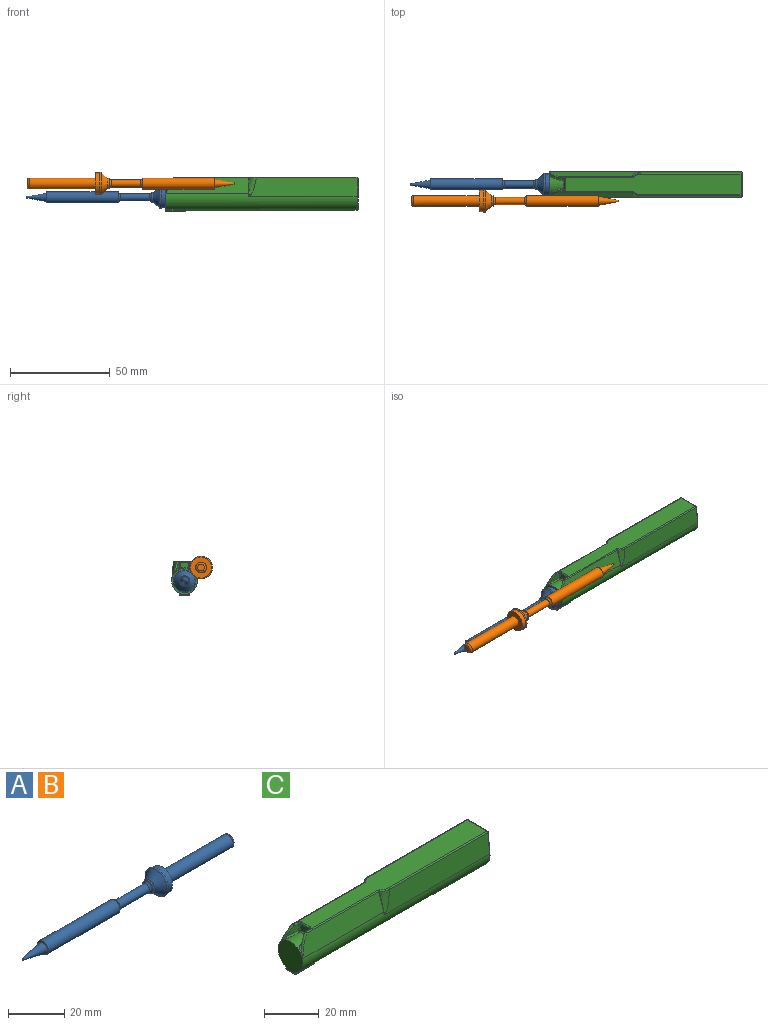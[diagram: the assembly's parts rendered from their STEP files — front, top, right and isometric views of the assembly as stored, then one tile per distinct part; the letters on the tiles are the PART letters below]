
ASSEMBLY  parts=3 mates=1
PART A: 15 faces, bbox 104.1x12.3x12.3 mm
  f0: plane 3.4x3.4mm, normal (1,0,0), area 9.1mm2, adj f12
  f1: cylinder r=2.7mm len=33mm, axis (1,0,0), area 559.8mm2, adj f2,f12
  f2: plane 10.6x10.6mm, normal (1,0,0), area 65.3mm2, adj f1,f3
  f3: cylinder r=5.3mm len=10.6mm, axis (1,0,0), area 74.9mm2, adj f2,f4
  f4: torus R=5.3mm, axis (1,0,0), area 43.9mm2, adj f3,f5
  f5: cone r=5.3mm half-angle=39.5deg, axis (1,0,0), area 104.8mm2, adj f4,f6
  f6: cylinder r=2.62mm len=5.25mm, axis (1,0,0), area 12.4mm2, adj f5,f13
  f7: cylinder r=1.8mm len=14.77mm, axis (1,0,0), area 167mm2, adj f13,f14
  f8: cylinder r=2.75mm len=36mm, axis (1,0,0), area 622mm2, adj f9,f14
  f9: plane 5.5x5.5mm, normal (-1,0,0), area 8.6mm2, adj f8,f10
  f10: cone r=2.2mm half-angle=10.3deg, axis (1,0,0), area 82.2mm2, adj f9,f11
  f11: sphere r=0.38mm, area 0.7mm2, adj f10
  f12: torus R=1.7mm, axis (-1,0,0), area 23.1mm2, adj f0,f1
  f13: torus R=2.8mm, axis (1,0,0), area 18.4mm2, adj f6,f7
  f14: torus R=2.8mm, axis (-1,0,0), area 20.5mm2, adj f7,f8
PART B: same geometry as A
PART C: 69 faces, bbox 98.5x14.5x21 mm
  f0: cylinder r=6.45mm len=96mm, axis (-1,0,0), area 2152.6mm2, adj f2,f4,f5,f6,f7,f8,f9,f11
  f1: plane 15.6x11.9mm, normal (1,0,0), area 162mm2, adj f46,f50,f52,f53
  f2: plane 13.25x12.9mm, normal (-1,0,0), area 132.7mm2, adj f0,f58,f64,f65
  f3: plane 9x4.25mm, normal (0,0,-1), area 38.2mm2, adj f59,f62,f65,f68
  f4: plane 9x0.91mm, normal (0,1,0), area 8.2mm2, adj f0,f63,f64,f68
  f5: plane 9x0.91mm, normal (0,-1,0), area 8.2mm2, adj f0,f57,f58,f59
  f6: plane 4.25x0.71mm, normal (1,0,0), area 2mm2, adj f0,f57,f62,f63
  f7: plane 41.55x7.98mm, normal (0,0.96,0.28), area 329.6mm2, adj f0,f20,f36,f37
  f8: plane 54.79x9.64mm, normal (0,-1,0.1), area 471.5mm2, adj f0,f14,f15,f53,f56
  f9: plane 54.25x9.1mm, normal (0,1,0.1), area 471.5mm2, adj f0,f12,f13,f45,f46
  f10: plane 91.14x10.09mm, normal (0,0,1), area 772.9mm2, adj f28,f31,f35,f36,f38,f39,f41,f42
  f11: plane 41.55x7.98mm, normal (0,-0.96,0.28), area 329.6mm2, adj f0,f19,f47,f48
  f12: bspline ~11.52x4.08mm, area 23.8mm2, adj f9,f13,f33,f37,f42
  f13: bspline ~1.61x0.7mm, area 0.2mm2, adj f9,f12,f29
  f14: bspline ~11.52x4.08mm, area 23.8mm2, adj f8,f15,f43,f47,f54
  f15: bspline ~1.61x0.7mm, area 0.2mm2, adj f8,f14,f40
  f16: plane 4.44x3.06mm, normal (-1,0,0), area 12.5mm2, adj f26,f27,f34,f35
  f17: cylinder r=10mm len=5.24mm, axis (0,0,1), area 12.3mm2, adj f19,f25,f34,f41
  f18: cylinder r=10mm len=5.24mm, axis (0,0,1), area 12.3mm2, adj f20,f22,f27,f28
  f19: bspline ~13.5x7.26mm, area 9.7mm2, adj f11,f17,f23,f44
  f20: bspline ~13.5x7.26mm, area 9.7mm2, adj f7,f18,f21,f32
  f21: bspline ~4.26x2.97mm, area 1.6mm2, adj f0,f20,f22
  f22: bspline ~5.95x2.06mm, area 5.4mm2, adj f0,f18,f21,f24
  f23: bspline ~4.26x2.97mm, area 1.6mm2, adj f0,f19,f25
  f24: sphere r=0.5mm, area 0.4mm2, adj f22,f26,f27
  f25: bspline ~5.95x2.06mm, area 5.4mm2, adj f0,f17,f23,f30
  f26: torus R=6.95mm, axis (-1,0,0), area 3.4mm2, adj f0,f16,f24,f30
  f27: cylinder r=0.5mm len=3.06mm, axis (0,0,1), area 2.5mm2, adj f16,f18,f24,f31
  f28: torus R=9.5mm, axis (0,0,-1), area 1.6mm2, adj f10,f18,f31,f32
  f29: bspline ~1.32x0.27mm, area 0mm2, adj f0,f13,f33
  f30: sphere r=0.5mm, area 0.5mm2, adj f25,f26,f34
  f31: torus R=1mm, axis (0,0,-1), area 0.9mm2, adj f10,f27,f28,f35
  f32: sphere r=0.5mm, area 0.3mm2, adj f20,f28,f36
  f33: bspline ~0.12x0.06mm, area 0mm2, adj f0,f12,f29,f37
  f34: cylinder r=0.5mm len=3.06mm, axis (0,0,1), area 2.5mm2, adj f16,f17,f30,f38
  f35: cylinder r=0.5mm len=4.44mm, axis (0,1,0), area 3.5mm2, adj f10,f16,f31,f38
  f36: cylinder r=0.5mm len=36.68mm, axis (-1,0,0), area 23.6mm2, adj f7,f10,f32,f39
  f37: bspline ~9.12x2.65mm, area 2.2mm2, adj f7,f12,f33,f39
  f38: torus R=1mm, axis (0,0,-1), area 0.9mm2, adj f10,f34,f35,f41
  f39: bspline ~1x0.74mm, area 0.4mm2, adj f10,f36,f37,f42
  f40: bspline ~1.2x0.23mm, area 0mm2, adj f0,f15,f43
  f41: torus R=9.5mm, axis (0,0,-1), area 1.6mm2, adj f10,f17,f38,f44
  f42: bspline ~4.69x2.2mm, area 2.7mm2, adj f10,f12,f39,f45
  f43: bspline ~0.13x0.06mm, area 0mm2, adj f0,f14,f40,f47
  f44: sphere r=0.5mm, area 0.1mm2, adj f19,f41,f48
  f45: cylinder r=0.5mm len=50.51mm, axis (-1,0,0), area 37.2mm2, adj f9,f10,f42,f49
  f46: cylinder r=0.5mm len=9.13mm, axis (0,-0.1,1), area 7.2mm2, adj f1,f9,f49,f50
  f47: bspline ~9.12x2.65mm, area 2.2mm2, adj f11,f14,f43,f51
  f48: cylinder r=0.5mm len=36.68mm, axis (1,0,0), area 23.6mm2, adj f10,f11,f44,f51
  f49: sphere r=0.5mm, area 0.2mm2, adj f45,f46,f52
  f50: torus R=5.95mm, axis (1,0,0), area 16.4mm2, adj f0,f1,f46,f53
  f51: bspline ~0.93x0.68mm, area 0.4mm2, adj f10,f47,f48,f54
  f52: cylinder r=0.5mm len=10.09mm, axis (0,-1,0), area 7.9mm2, adj f1,f10,f49,f55
  f53: cylinder r=0.5mm len=9.13mm, axis (0,-0.1,-1), area 7.2mm2, adj f1,f8,f50,f55
  f54: bspline ~4.69x2.21mm, area 2.7mm2, adj f10,f14,f51,f56
  f55: sphere r=0.5mm, area 0.4mm2, adj f52,f53,f56
  f56: cylinder r=0.5mm len=50.51mm, axis (1,0,0), area 37.2mm2, adj f8,f10,f54,f55
  f57: cylinder r=0.5mm len=0.91mm, axis (0,0,1), area 0.6mm2, adj f0,f5,f6,f60
  f58: cylinder r=0.5mm len=0.91mm, axis (0,0,-1), area 0.6mm2, adj f0,f2,f5,f61
  f59: cylinder r=0.5mm len=9mm, axis (1,0,0), area 7.1mm2, adj f3,f5,f60,f61
  f60: sphere r=0.5mm, area 0.4mm2, adj f57,f59,f62
  f61: sphere r=0.5mm, area 0.4mm2, adj f58,f59,f65
  f62: cylinder r=0.5mm len=4.25mm, axis (0,-1,0), area 3.3mm2, adj f3,f6,f60,f66
  f63: cylinder r=0.5mm len=0.91mm, axis (0,0,-1), area 0.6mm2, adj f0,f4,f6,f66
  f64: cylinder r=0.5mm len=0.91mm, axis (0,0,1), area 0.6mm2, adj f0,f2,f4,f67
  f65: cylinder r=0.5mm len=4.25mm, axis (0,1,0), area 3.3mm2, adj f2,f3,f61,f67
  f66: sphere r=0.5mm, area 0.2mm2, adj f62,f63,f68
  f67: sphere r=0.5mm, area 0.5mm2, adj f64,f65,f68
  f68: cylinder r=0.5mm len=9mm, axis (-1,0,0), area 7.1mm2, adj f3,f4,f66,f67
PLACE A t=(0,8.86,0.93)mm
PLACE B rot(axis=(0,0,1),180deg) t=(-35.41,0.54,7.83)mm
PLACE C t=(0,8.86,0.93)mm
MATE fastened C.f0 <-> A.f5  axis (-1,0,0) through (0,8.86,0.93)mm
